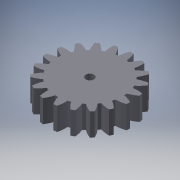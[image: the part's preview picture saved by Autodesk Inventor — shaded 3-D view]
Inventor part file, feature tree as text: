
AUTODESK INVENTOR PART (.ipt)
format: ipt  version: 2016 (Build 200138000, 138)  size: 224,256 bytes
history: native  units: mm (DEFAULTED — no unit token found)
features: sketch x4, plane x3, other x3, extrude x2
ambient origin geometry x8: Origin, YZ Plane, XZ Plane, XY Plane, X Axis, Y Axis, Z Axis, Center Point
bodies: Solid1 (feature_tree)
feature tree (12):
  extrude  "Extrusion1"  Depth=15.0mm TaperAngle=0.0deg
  plane  "Work Plane2"
  plane  "Work Plane8"
  plane  "Work Plane9"
  other  "Spur Gear"
  extrude  "Extrusion2"  Depth=10.0mm TaperAngle=0.0deg
  sketch  "Sketch4"  dims[d17=0.0mm d34=1.65347mm d39=0.0mm d41=0.0mm d43=100.7mm d46=100.7mm d47=0.0mm d48=0.0mm d49=5.5mm d50=10.0mm d51=0.0mm]
  sketch  "Sketch1"  dims[d0=55.65mm d1=15.0mm d2=0.0mm]
  sketch  "Sketch2"  dims[d3=50.35mm d4=10.0mm d5=0.0mm]
  other  "Srf1"
  sketch  "Sketch3"  dims[d16=100.7mm]
  other  "Pitch Diameter"
